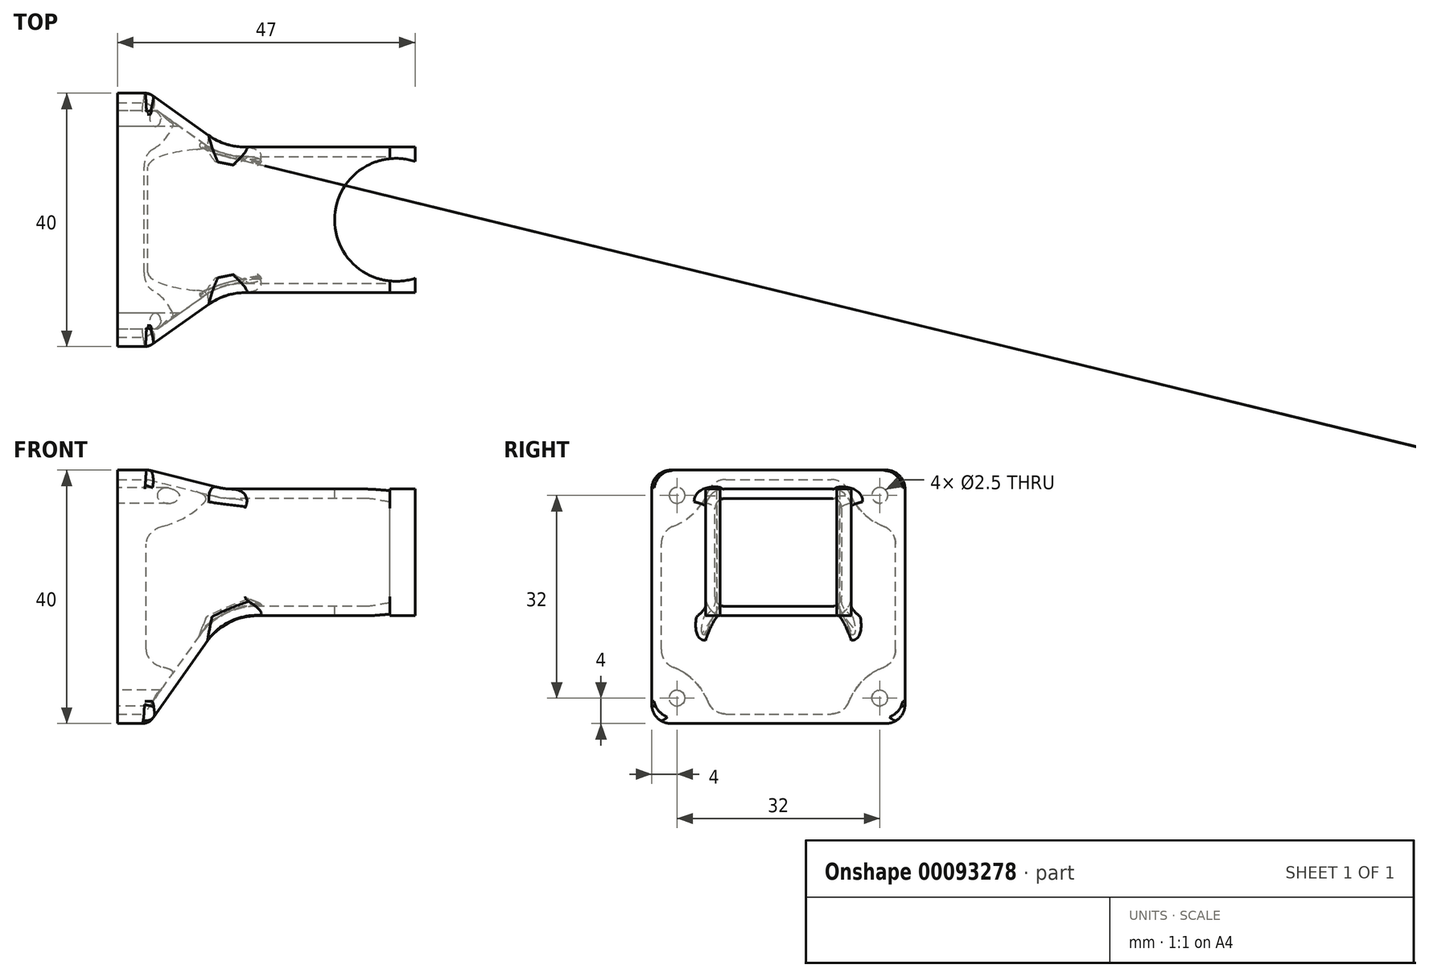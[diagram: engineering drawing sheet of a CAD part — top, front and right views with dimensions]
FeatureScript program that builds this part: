
annotation { "Feature Type Name" : "Feature", "Feature Type Description" : "" }
export const myFeature = defineFeature(function(context is Context, id is Id, definition is map)
    precondition{}
    {
        {
            var Q0;
            Q0=qCreatedBy(makeId("Front.planeOp"),FACE);
            var sketch = newSketch(context, id + "F0", { "sketchPlane" : qUnion([Q0])});
            skLineSegment(sketch, "E0.bottom", {"start": v(15, -10) * mm, "end": v(-15, -10) * mm});
            skLineSegment(sketch, "E0.top", {"start": v(15, 10) * mm, "end": v(-15, 10) * mm});
            skLineSegment(sketch, "E0.left", {"start": v(15, -10) * mm, "end": v(15, 10) * mm});
            skLineSegment(sketch, "E0.right", {"start": v(-15, -10) * mm, "end": v(-15, 10) * mm});
            skPoint(sketch, "E0.middle", {"position": v(0, 0) * mm});
            skSolve(sketch);
        }
        {
            var Q0;
            Q0=qSketchRegion(id+"F0",true);
            extrude(context, id + "F1", {"entities" : qUnion([Q0]), "endBound" : BoundingType.SYMMETRIC, "depth" : 23 * mm});
        }
        {
            var Q0;
            Q0=makeQuery(id+"F1.opExtrude","SWEPT_FACE",FACE,{"disambiguationData":[OSD([sQuery(id+"F0.wireOp",EDGE,"E0.right")])]});
            cPlane(context, id + "F2", {"entities" : qUnion([Q0]), "cplaneType" : CPlaneType.OFFSET, "offset" : 12 * mm, "width" : 150 * mm, "height" : 150 * mm});
        }
        {
            var Q0;
            Q0=qCreatedBy(id+"F2.planeOp",FACE);
            var sketch = newSketch(context, id + "F3", { "sketchPlane" : qUnion([Q0])});
            skLineSegment(sketch, "E1.bottom", {"start": v(20, -27) * mm, "end": v(-20, -27) * mm});
            skLineSegment(sketch, "E1.top", {"start": v(20, 13) * mm, "end": v(-20, 13) * mm});
            skLineSegment(sketch, "E1.left", {"start": v(20, -27) * mm, "end": v(20, 13) * mm});
            skLineSegment(sketch, "E1.right", {"start": v(-20, -27) * mm, "end": v(-20, 13) * mm});
            skPoint(sketch, "E1.middle", {"position": v(0, -7) * mm});
            skSolve(sketch);
        }
        {
            var Q1;
            Q1=makeQuery(id+"F1.opExtrude","SWEPT_FACE",FACE,{"disambiguationData":[OSD([sQuery(id+"F0.wireOp",EDGE,"E0.right")])]});
            var Q2;
            Q2=makeQuery(id+"F3.imprint","IMPRINT",FACE,{"disambiguationData":[TD([[makeQuery(id+"F3.imprint","IMPRINT",EDGE,{"derivedFrom":sQuery(id+"F3.wireOp",EDGE,"E1.bottom")}),-1.0]])]});
            loft(context, id + "F4", {"operationType" : NewBodyOperationType.ADD, "sheetProfilesArray" : [{ "sheetProfileEntities" : qUnion([Q1]) }, { "sheetProfileEntities" : qUnion([Q2]) }]});
        }
        {
            var Q0;
            Q0=makeQuery(id+"F4.opLoft","CAP_FACE",FACE,{"disambiguationData":[OSD([makeQuery(id+"F3.imprint","IMPRINT",FACE,{"disambiguationData":[TD([[makeQuery(id+"F3.imprint","IMPRINT",EDGE,{"derivedFrom":sQuery(id+"F3.wireOp",EDGE,"E1.bottom")}),-1.0]])]})])],"isStart":true});
            var sketch = newSketch(context, id + "F5", { "sketchPlane" : qUnion([Q0])});
            skLineSegment(sketch, "E2.bottom", {"start": v(-20, 13) * mm, "end": v(20, 13) * mm});
            skLineSegment(sketch, "E2.top", {"start": v(-20, -27) * mm, "end": v(20, -27) * mm});
            skLineSegment(sketch, "E2.left", {"start": v(-20, 13) * mm, "end": v(-20, -27) * mm});
            skLineSegment(sketch, "E2.right", {"start": v(20, 13) * mm, "end": v(20, -27) * mm});
            skSolve(sketch);
        }
        {
            var Q0;
            Q0=qSketchRegion(id+"F5",true);
            extrude(context, id + "F6", {"entities" : qUnion([Q0]), "operationType" : NewBodyOperationType.ADD, "depth" : 5 * mm});
        }
        {
            var Q0;
            {var subQ1=sQuery(id+"F0.wireOp",EDGE,"E0.left");var subQ2=sQuery(id+"F0.wireOp",EDGE,"E0.top");Q0=makeQuery(id+"Fz8CBDRqYWuNpRD_1.boolean.opBoolean","SPLIT",EDGE,{"disambiguationData":[TD([makeQuery(id+"F1.opExtrude","SWEPT_FACE",FACE,{"disambiguationData":[OSD([subQ1])]})])],"derivedFrom":makeQuery(id+"F1.opExtrude","CAP_EDGE",EDGE,{"disambiguationData":[OSD([subQ2])],"isStart":false})});}
            var Q1;
            Q1=makeQuery(id+"F1.opExtrude","CAP_EDGE",EDGE,{"disambiguationData":[OSD([sQuery(id+"F0.wireOp",EDGE,"E0.bottom")])],"isStart":false});
            var Q2;
            {var subQ0=sQuery(id+"F0.wireOp",EDGE,"E0.left");var subQ1=sQuery(id+"F0.wireOp",EDGE,"E0.top");Q2=makeQuery(id+"Fz8CBDRqYWuNpRD_1.boolean.opBoolean","SPLIT",EDGE,{"disambiguationData":[TD([makeQuery(id+"F1.opExtrude","SWEPT_FACE",FACE,{"disambiguationData":[OSD([subQ0])]})])],"derivedFrom":makeQuery(id+"F1.opExtrude","CAP_EDGE",EDGE,{"disambiguationData":[OSD([subQ1])],"isStart":true})});}
            var Q3;
            Q3=makeQuery(id+"F1.opExtrude","CAP_EDGE",EDGE,{"disambiguationData":[OSD([sQuery(id+"F0.wireOp",EDGE,"E0.bottom")])],"isStart":true});
            var Q4;
            Q4=makeQuery(id+"F4.opLoft","SWEPT_EDGE",EDGE,{"disambiguationData":[OSD([sQuery(id+"F0.wireOp",EDGE,"E0.bottom"),sQuery(id+"F0.wireOp",EDGE,"E0.right"),sQuery(id+"F3.wireOp",EDGE,"E1.bottom"),sQuery(id+"F3.wireOp",EDGE,"E1.right")])]});
            var Q5;
            Q5=makeQuery(id+"F4.opLoft","SWEPT_EDGE",EDGE,{"disambiguationData":[OSD([sQuery(id+"F0.wireOp",EDGE,"E0.bottom"),sQuery(id+"F0.wireOp",EDGE,"E0.right"),sQuery(id+"F3.wireOp",EDGE,"E1.bottom"),sQuery(id+"F3.wireOp",EDGE,"E1.left")])]});
            var Q6;
            Q6=makeQuery(id+"F4.opLoft","SWEPT_EDGE",EDGE,{"disambiguationData":[OSD([sQuery(id+"F0.wireOp",EDGE,"E0.top"),sQuery(id+"F0.wireOp",EDGE,"E0.right"),sQuery(id+"F3.wireOp",EDGE,"E1.top"),sQuery(id+"F3.wireOp",EDGE,"E1.left")])]});
            var Q7;
            Q7=makeQuery(id+"F4.opLoft","SWEPT_EDGE",EDGE,{"disambiguationData":[OSD([sQuery(id+"F0.wireOp",EDGE,"E0.top"),sQuery(id+"F0.wireOp",EDGE,"E0.right"),sQuery(id+"F3.wireOp",EDGE,"E1.top"),sQuery(id+"F3.wireOp",EDGE,"E1.right")])]});
            var Q8;
            {var subQ1=sQuery(id+"F0.wireOp",EDGE,"E0.right");var subQ2=sQuery(id+"F0.wireOp",EDGE,"E0.top");Q8=makeQuery(id+"Fz8CBDRqYWuNpRD_1.boolean.opBoolean","SPLIT",EDGE,{"disambiguationData":[TD([makeQuery(id+"F1.opExtrude","SWEPT_FACE",FACE,{"disambiguationData":[OSD([subQ1])]})])],"derivedFrom":makeQuery(id+"F1.opExtrude","CAP_EDGE",EDGE,{"disambiguationData":[OSD([subQ2])],"isStart":false})});}
            var Q9;
            {var subQ1=sQuery(id+"F0.wireOp",EDGE,"E0.right");var subQ2=sQuery(id+"F0.wireOp",EDGE,"E0.top");Q9=makeQuery(id+"Fz8CBDRqYWuNpRD_1.boolean.opBoolean","SPLIT",EDGE,{"disambiguationData":[TD([makeQuery(id+"F1.opExtrude","SWEPT_FACE",FACE,{"disambiguationData":[OSD([subQ1])]})])],"derivedFrom":makeQuery(id+"F1.opExtrude","CAP_EDGE",EDGE,{"disambiguationData":[OSD([subQ2])],"isStart":true})});}
            fillet(context, id + "F7", {"entities" : qUnion([Q0, Q1, Q2, Q3, Q4, Q5, Q6, Q7, Q8, Q9]), "radius" : 3 * mm, "tangentPropagation" : true, "allowEdgeOverflow" : false});
        }
        {
            var Q0;
            {var subQ0=sQuery(id+"F0.wireOp",EDGE,"E0.right");var subQ1=sQuery(id+"F0.wireOp",EDGE,"E0.top");Q0=makeQuery(id+"F4.boolean.opBoolean","MERGE",EDGE,{"derivedFrom":[makeQuery(id+"F1.opExtrude","SWEPT_EDGE",EDGE,{"disambiguationData":[OSD([subQ1,subQ0])]}),makeQuery(id+"F4.opLoft","MID_CAP_EDGE",EDGE,{"disambiguationData":[OSD([subQ1,subQ0])],"capPos":0.0})]});}
            fillet(context, id + "F8", {"entities" : qUnion([Q0]), "radius" : 10 * mm, "tangentPropagation" : true, "allowEdgeOverflow" : false});
        }
        {
            var Q0;
            Q0=makeQuery(id+"F6.opExtrude","CAP_FACE",FACE,{"disambiguationData":[OSD([sQuery(id+"F5.wireOp",EDGE,"E2.bottom"),sQuery(id+"F5.wireOp",EDGE,"E2.top"),sQuery(id+"F5.wireOp",EDGE,"E2.left"),sQuery(id+"F5.wireOp",EDGE,"E2.right")])],"isStart":false});
            var Q1;
            Q1=makeQuery(id+"F13.boolean.opBoolean","COPY",FACE,{"derivedFrom":makeQuery(id+"F13.opExtrude","SWEPT_FACE",FACE,{"disambiguationData":[OSD([sQuery(id+"F12.wireOp",EDGE,"E8")])]})});
            var Q2;
            Q2=makeQuery(id+"F1.opExtrude","SWEPT_FACE",FACE,{"disambiguationData":[OSD([sQuery(id+"F0.wireOp",EDGE,"E0.left")])]});
            shell(context, id + "F9", {"entities" : qUnion([Q0, Q1, Q2]), "thickness" : 1.5 * mm});
        }
        {
            var Q0;
            Q0=makeQuery(id+"F1.opExtrude","SWEPT_FACE",FACE,{"disambiguationData":[OSD([sQuery(id+"F0.wireOp",EDGE,"E0.top")])]});
            var sketch = newSketch(context, id + "F10", { "sketchPlane" : qUnion([Q0])});
            skLineSegment(sketch, "E3.bottom", {"start": v(11, 11.5) * mm, "end": v(15, 11.5) * mm});
            skLineSegment(sketch, "E3.top", {"start": v(11, 8.5) * mm, "end": v(15, 8.5) * mm});
            skLineSegment(sketch, "E3.left", {"start": v(11, 11.5) * mm, "end": v(11, 8.5) * mm});
            skLineSegment(sketch, "E3.right", {"start": v(15, 11.5) * mm, "end": v(15, 8.5) * mm});
            skLineSegment(sketch, "E4.MirrorCS", {"start": v(11, -11.5) * mm, "end": v(15, -11.5) * mm});
            skLineSegment(sketch, "E5.MirrorCS", {"start": v(15, -11.5) * mm, "end": v(15, -8.5) * mm});
            skLineSegment(sketch, "E6.MirrorCS", {"start": v(11, -11.5) * mm, "end": v(11, -8.5) * mm});
            skLineSegment(sketch, "E7.MirrorCS", {"start": v(11, -8.5) * mm, "end": v(15, -8.5) * mm});
            skSolve(sketch);
        }
        {
            var Q0;
            Q0 = qSketchRegion(id + "F10", true);
            var Q1;
            Q1=makeQuery(id+"F1.opExtrude","SWEPT_FACE",FACE,{"disambiguationData":[OSD([sQuery(id+"F0.wireOp",EDGE,"E0.bottom")])]});
            extrude(context, id + "F11", {"entities" : qUnion([Q0]), "operationType" : NewBodyOperationType.ADD, "endBound" : BoundingType.UP_TO_SURFACE, "oppositeDirection" : true, "endBoundEntityFace" : qUnion([Q1]), "depth" : 25 * mm});
        }
        {
            var Q0;
            Q0=makeQuery(id+"F1.opExtrude","SWEPT_FACE",FACE,{"disambiguationData":[OSD([sQuery(id+"F0.wireOp",EDGE,"E0.top")])]});
            var sketch = newSketch(context, id + "F12", { "sketchPlane" : qUnion([Q0])});
            skCircle(sketch, "E8", {"center": v(12, 0) * mm, "radius": 9.7 * mm});
            skSolve(sketch);
        }
        {
            var Q0;
            Q0=qSketchRegion(id+"F12",true);
            extrude(context, id + "F13", {"entities" : qUnion([Q0]), "operationType" : NewBodyOperationType.REMOVE, "endBound" : BoundingType.THROUGH_ALL, "oppositeDirection" : true, "depth" : 25 * mm});
        }
        {
            var Q0;
            Q0=makeQuery(id+"F6.opExtrude","CAP_FACE",FACE,{"disambiguationData":[OSD([sQuery(id+"F5.wireOp",EDGE,"E2.bottom"),sQuery(id+"F5.wireOp",EDGE,"E2.top"),sQuery(id+"F5.wireOp",EDGE,"E2.left"),sQuery(id+"F5.wireOp",EDGE,"E2.right")])],"isStart":false});
            var sketch = newSketch(context, id + "F14", { "sketchPlane" : qUnion([Q0])});
            skLineSegment(sketch, "E9", {"start": v(16, 9) * mm, "end": v(16, -23) * mm, "construction": true});
            skLineSegment(sketch, "E10", {"start": v(16, -23) * mm, "end": v(-16, -23) * mm, "construction": true});
            skCircle(sketch, "E11", {"center": v(16, 9) * mm, "radius": 1.25 * mm});
            skCircle(sketch, "E12", {"center": v(16, -23) * mm, "radius": 1.25 * mm});
            skCircle(sketch, "E13", {"center": v(-16, -23) * mm, "radius": 1.25 * mm});
            skCircle(sketch, "E14", {"center": v(-16, 9) * mm, "radius": 1.25 * mm});
            skArc(sketch, "E15", {"start": v(-20, 3.5) * mm, "mid": v(-13.28, 6.28) * mm, "end": v(-10.5, 13) * mm});
            skArc(sketch, "E16", {"start": v(10.5, 13) * mm, "mid": v(13.28, 6.28) * mm, "end": v(20, 3.5) * mm});
            skArc(sketch, "E17", {"start": v(20, -17.5) * mm, "mid": v(13.28, -20.28) * mm, "end": v(10.5, -27) * mm});
            skArc(sketch, "E18", {"start": v(-10.5, -27) * mm, "mid": v(-13.28, -20.28) * mm, "end": v(-20, -17.5) * mm});
            skLineSegment(sketch, "E19", {"start": v(10.5, 13) * mm, "end": v(20, 13) * mm});
            skLineSegment(sketch, "E20", {"start": v(20, -17.5) * mm, "end": v(20, -27) * mm});
            skLineSegment(sketch, "E21", {"start": v(-20, 3.5) * mm, "end": v(-20, 13) * mm});
            skLineSegment(sketch, "E22", {"start": v(-20, 13) * mm, "end": v(-10.5, 13) * mm});
            skLineSegment(sketch, "E23", {"start": v(20, 13) * mm, "end": v(20, 3.5) * mm});
            skLineSegment(sketch, "E24", {"start": v(20, -27) * mm, "end": v(10.5, -27) * mm});
            skLineSegment(sketch, "E25", {"start": v(-10.5, -27) * mm, "end": v(-20, -27) * mm});
            skLineSegment(sketch, "E26", {"start": v(-20, -27) * mm, "end": v(-20, -17.5) * mm});
            skSolve(sketch);
        }
        {
            var Q0;
            Q0=qSketchRegion(id+"F14",true);
            var Q1;
            Q1=makeQuery(id+"F1.opExtrude","SWEPT_BODY",BODY,{"disambiguationData":[OSD([sQuery(id+"F0.wireOp",EDGE,"E0.bottom"),sQuery(id+"F0.wireOp",EDGE,"E0.top"),sQuery(id+"F0.wireOp",EDGE,"E0.left"),sQuery(id+"F0.wireOp",EDGE,"E0.right")])]});
            extrude(context, id + "F15", {"entities" : qUnion([Q0]), "operationType" : NewBodyOperationType.ADD, "endBound" : BoundingType.UP_TO_BODY, "oppositeDirection" : true, "endBoundEntityBody" : qUnion([Q1]), "depth" : 5 * mm});
        }
        {
            var Q0;
            Q0=makeQuery(id+"F15.boolean.opBoolean","MERGE",EDGE,{"derivedFrom":[makeQuery(id+"F6.opExtrude","SWEPT_EDGE",EDGE,{"disambiguationData":[OSD([sQuery(id+"F5.wireOp",EDGE,"E2.top"),sQuery(id+"F5.wireOp",EDGE,"E2.left")])]}),makeQuery(id+"F15.opExtrude","SWEPT_EDGE",EDGE,{"disambiguationData":[OSD([sQuery(id+"F14.wireOp",EDGE,"E25"),sQuery(id+"F14.wireOp",EDGE,"E26")])]})]});
            var Q1;
            Q1=makeQuery(id+"F15.boolean.opBoolean","MERGE",EDGE,{"derivedFrom":[makeQuery(id+"F6.opExtrude","SWEPT_EDGE",EDGE,{"disambiguationData":[OSD([sQuery(id+"F5.wireOp",EDGE,"E2.bottom"),sQuery(id+"F5.wireOp",EDGE,"E2.left")])]}),makeQuery(id+"F15.opExtrude","SWEPT_EDGE",EDGE,{"disambiguationData":[OSD([sQuery(id+"F14.wireOp",EDGE,"E21"),sQuery(id+"F14.wireOp",EDGE,"E22")])]})]});
            var Q2;
            Q2=makeQuery(id+"F15.boolean.opBoolean","MERGE",EDGE,{"derivedFrom":[makeQuery(id+"F6.opExtrude","SWEPT_EDGE",EDGE,{"disambiguationData":[OSD([sQuery(id+"F5.wireOp",EDGE,"E2.top"),sQuery(id+"F5.wireOp",EDGE,"E2.right")])]}),makeQuery(id+"F15.opExtrude","SWEPT_EDGE",EDGE,{"disambiguationData":[OSD([sQuery(id+"F14.wireOp",EDGE,"E20"),sQuery(id+"F14.wireOp",EDGE,"E24")])]})]});
            var Q3;
            Q3=makeQuery(id+"F15.boolean.opBoolean","MERGE",EDGE,{"derivedFrom":[makeQuery(id+"F6.opExtrude","SWEPT_EDGE",EDGE,{"disambiguationData":[OSD([sQuery(id+"F5.wireOp",EDGE,"E2.bottom"),sQuery(id+"F5.wireOp",EDGE,"E2.right")])]}),makeQuery(id+"F15.opExtrude","SWEPT_EDGE",EDGE,{"disambiguationData":[OSD([sQuery(id+"F14.wireOp",EDGE,"E19"),sQuery(id+"F14.wireOp",EDGE,"E23")])]})]});
            fillet(context, id + "F16", {"entities" : qUnion([Q0, Q1, Q2, Q3]), "radius" : 3 * mm, "tangentPropagation" : true, "allowEdgeOverflow" : false});
        }
        {
            var Q0;
            Q0=makeQuery(id+"F6.boolean.opBoolean","MERGE",EDGE,{"derivedFrom":[makeQuery(id+"F4.opLoft","MID_CAP_EDGE",EDGE,{"disambiguationData":[OSD([sQuery(id+"F3.wireOp",EDGE,"E1.bottom"),sQuery(id+"F3.wireOp",EDGE,"E1.left"),sQuery(id+"F3.wireOp",EDGE,"E1.right")])],"capPos":1.0}),makeQuery(id+"F6.opExtrude","CAP_EDGE",EDGE,{"disambiguationData":[OSD([sQuery(id+"F5.wireOp",EDGE,"E2.top")])],"isStart":true})]});
            fillet(context, id + "F17", {"entities" : qUnion([Q0]), "radius" : 2 * mm, "tangentPropagation" : true, "allowEdgeOverflow" : false});
        }
        {
            var Q0;
            Q0=makeQuery(id+"F15.boolean.opBoolean","INTERSECT",EDGE,{"derivedFrom":[makeQuery(id+"F9.opShell","OFFSET_FACE",FACE,{"disambiguationData":[OSD([sQuery(id+"F5.wireOp",EDGE,"E2.left")])]}),makeQuery(id+"F15.opExtrude","SWEPT_FACE",FACE,{"disambiguationData":[OSD([sQuery(id+"F14.wireOp",EDGE,"E15")])]})]});
            var Q1;
            Q1=makeQuery(id+"F15.boolean.opBoolean","INTERSECT",EDGE,{"derivedFrom":[makeQuery(id+"F9.opShell","OFFSET_FACE",FACE,{"disambiguationData":[OSD([sQuery(id+"F5.wireOp",EDGE,"E2.bottom")])]}),makeQuery(id+"F15.opExtrude","SWEPT_FACE",FACE,{"disambiguationData":[OSD([sQuery(id+"F14.wireOp",EDGE,"E15")])]})]});
            var Q2;
            Q2=makeQuery(id+"F15.boolean.opBoolean","INTERSECT",EDGE,{"derivedFrom":[makeQuery(id+"F9.opShell","OFFSET_FACE",FACE,{"disambiguationData":[OSD([sQuery(id+"F5.wireOp",EDGE,"E2.bottom")])]}),makeQuery(id+"F15.opExtrude","SWEPT_FACE",FACE,{"disambiguationData":[OSD([sQuery(id+"F14.wireOp",EDGE,"E16")])]})]});
            var Q3;
            Q3=makeQuery(id+"F15.boolean.opBoolean","INTERSECT",EDGE,{"derivedFrom":[makeQuery(id+"F9.opShell","OFFSET_FACE",FACE,{"disambiguationData":[OSD([sQuery(id+"F5.wireOp",EDGE,"E2.right")])]}),makeQuery(id+"F15.opExtrude","SWEPT_FACE",FACE,{"disambiguationData":[OSD([sQuery(id+"F14.wireOp",EDGE,"E16")])]})]});
            var Q4;
            Q4=makeQuery(id+"F15.boolean.opBoolean","INTERSECT",EDGE,{"derivedFrom":[makeQuery(id+"F9.opShell","OFFSET_FACE",FACE,{"disambiguationData":[OSD([sQuery(id+"F5.wireOp",EDGE,"E2.right")])]}),makeQuery(id+"F15.opExtrude","SWEPT_FACE",FACE,{"disambiguationData":[OSD([sQuery(id+"F14.wireOp",EDGE,"E17")])]})]});
            var Q5;
            Q5=makeQuery(id+"F15.boolean.opBoolean","INTERSECT",EDGE,{"derivedFrom":[makeQuery(id+"F9.opShell","OFFSET_FACE",FACE,{"disambiguationData":[OSD([sQuery(id+"F5.wireOp",EDGE,"E2.top")])]}),makeQuery(id+"F15.opExtrude","SWEPT_FACE",FACE,{"disambiguationData":[OSD([sQuery(id+"F14.wireOp",EDGE,"E17")])]})]});
            var Q6;
            Q6=makeQuery(id+"F15.boolean.opBoolean","INTERSECT",EDGE,{"derivedFrom":[makeQuery(id+"F9.opShell","OFFSET_FACE",FACE,{"disambiguationData":[OSD([sQuery(id+"F5.wireOp",EDGE,"E2.top")])]}),makeQuery(id+"F15.opExtrude","SWEPT_FACE",FACE,{"disambiguationData":[OSD([sQuery(id+"F14.wireOp",EDGE,"E18")])]})]});
            var Q7;
            Q7=makeQuery(id+"F15.boolean.opBoolean","INTERSECT",EDGE,{"derivedFrom":[makeQuery(id+"F9.opShell","OFFSET_FACE",FACE,{"disambiguationData":[OSD([sQuery(id+"F5.wireOp",EDGE,"E2.left")])]}),makeQuery(id+"F15.opExtrude","SWEPT_FACE",FACE,{"disambiguationData":[OSD([sQuery(id+"F14.wireOp",EDGE,"E18")])]})]});
            fillet(context, id + "F18", {"entities" : qUnion([Q0, Q1, Q2, Q3, Q4, Q5, Q6, Q7]), "radius" : 3 * mm, "tangentPropagation" : true, "allowEdgeOverflow" : false});
        }
    });
